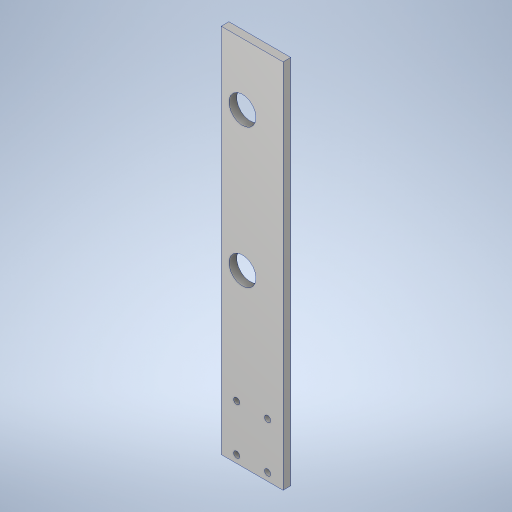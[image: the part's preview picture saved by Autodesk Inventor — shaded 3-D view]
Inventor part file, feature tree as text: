
AUTODESK INVENTOR PART (.ipt)
format: ipt  version: 2023.4 (Build 274418000, 418)  size: 265,728 bytes
history: native  units: in
note: dims shown in document units (in); Inventor stores cm internally (conversion verified against a paired STEP export)
features: sketch x2, extrude x1, hole x1
ambient origin geometry x8: Origin, YZ Plane, XZ Plane, XY Plane, X Axis, Y Axis, Z Axis, Center Point
bodies: Solid1 (feature_tree)
feature tree (4):
  extrude  "Extrusion1"  Depth=12.0in
  hole  "Hole1"  [1 undecoded]
  sketch  "Sketch1"  dims[d0=2.0in d1=12.0in]
  sketch  "Sketch2"  dims[d3=2.0in d4=0.875in d7=0.6875in d8=3.0in d9=4.0in d10=2.0in d11=0.875in d12=3.0in d13=4.0in d14=4.5in d15=5.5in d16=0.25in d17=0.0in d19=1.0in d21=1.5in d22=0.25in d23=0.201in d24=0.75in d25=0.385in d26=0.25in d27=0.5635in d28=1.0in d29=0.8108in d2=0.5in d5=0.0344in]
note: 1 required parameter value undecoded (feature->parameter linkage not recoverable at this tier; creation-order binding heuristic only, values carry confidence <= 0.55)
